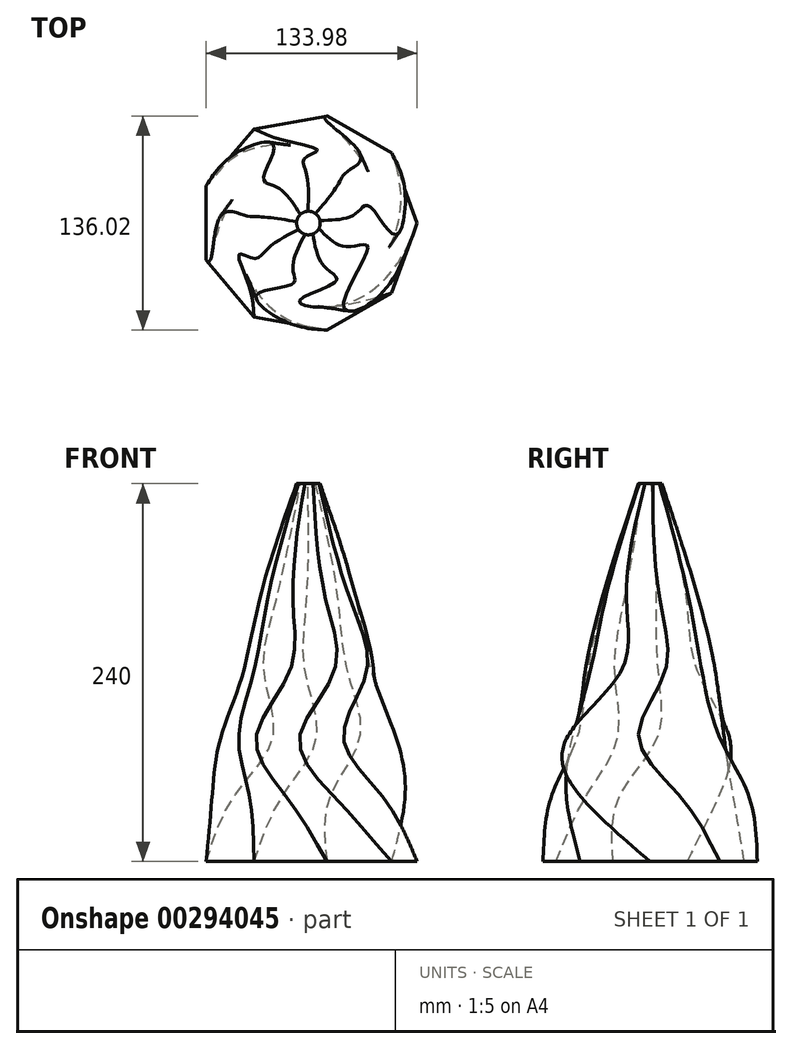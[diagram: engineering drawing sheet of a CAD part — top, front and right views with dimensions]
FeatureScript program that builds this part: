
annotation { "Feature Type Name" : "Feature", "Feature Type Description" : "" }
export const myFeature = defineFeature(function(context is Context, id is Id, definition is map)
    precondition{}
    {
        {
            var Q0;
            Q0=qCreatedBy(makeId("Top.planeOp"),FACE);
            cPlane(context, id + "F0", {"entities" : qUnion([Q0]), "cplaneType" : CPlaneType.OFFSET, "offset" : 40 * mm, "width" : 150 * mm, "height" : 150 * mm});
        }
        {
            var Q0;
            Q0=qCreatedBy(id+"F0.planeOp",FACE);
            cPlane(context, id + "F1", {"entities" : qUnion([Q0]), "cplaneType" : CPlaneType.OFFSET, "offset" : 40 * mm, "width" : 150 * mm, "height" : 150 * mm});
        }
        {
            var Q0;
            Q0=qCreatedBy(id+"F1.planeOp",FACE);
            cPlane(context, id + "F2", {"entities" : qUnion([Q0]), "cplaneType" : CPlaneType.OFFSET, "offset" : 40 * mm, "width" : 150 * mm, "height" : 150 * mm});
        }
        {
            var Q0;
            Q0=qCreatedBy(makeId("Top.planeOp"),FACE);
            var sketch = newSketch(context, id + "F3", { "sketchPlane" : qUnion([Q0])});
            skCircle(sketch, "E0.cCircle", {"center": v(0, 0) * mm, "radius": 64.9 * mm, "construction": true});
            skLineSegment(sketch, "E0.0", {"start": v(12.06, 68) * mm, "end": v(52.95, 44.34) * mm});
            skLineSegment(sketch, "E0.1", {"start": v(52.95, 44.34) * mm, "end": v(69.06, -0.07) * mm});
            skLineSegment(sketch, "E0.2", {"start": v(69.06, -0.07) * mm, "end": v(52.86, -44.45) * mm});
            skLineSegment(sketch, "E0.3", {"start": v(52.86, -44.45) * mm, "end": v(11.92, -68.02) * mm});
            skLineSegment(sketch, "E0.4", {"start": v(11.92, -68.02) * mm, "end": v(-34.6, -59.77) * mm});
            skLineSegment(sketch, "E0.5", {"start": v(-34.6, -59.77) * mm, "end": v(-64.92, -23.55) * mm});
            skLineSegment(sketch, "E0.6", {"start": v(-64.92, -23.55) * mm, "end": v(-64.87, 23.69) * mm});
            skLineSegment(sketch, "E0.7", {"start": v(-64.87, 23.69) * mm, "end": v(-34.47, 59.84) * mm});
            skLineSegment(sketch, "E0.8", {"start": v(-34.47, 59.84) * mm, "end": v(12.06, 68) * mm});
            skPoint(sketch, "E0.0.midPoint", {"position": v(32.5, 56.17) * mm});
            skSolve(sketch);
        }
        {
            var Q0;
            Q0=qCreatedBy(id+"F0.planeOp",FACE);
            var sketch = newSketch(context, id + "F4", { "sketchPlane" : qUnion([Q0])});
            skCircle(sketch, "E1.cCircle", {"center": v(0, 0) * mm, "radius": 55.87 * mm, "construction": true});
            skLineSegment(sketch, "E1.0", {"start": v(13.21, 63.15) * mm, "end": v(61.3, 20.13) * mm});
            skLineSegment(sketch, "E1.1", {"start": v(61.3, 20.13) * mm, "end": v(48.08, -43.02) * mm});
            skLineSegment(sketch, "E1.2", {"start": v(48.08, -43.02) * mm, "end": v(-13.21, -63.15) * mm});
            skLineSegment(sketch, "E1.3", {"start": v(-13.21, -63.15) * mm, "end": v(-61.3, -20.13) * mm});
            skLineSegment(sketch, "E1.4", {"start": v(-61.3, -20.13) * mm, "end": v(-48.08, 43.02) * mm});
            skLineSegment(sketch, "E1.5", {"start": v(-48.08, 43.02) * mm, "end": v(13.21, 63.15) * mm});
            skPoint(sketch, "E1.0.midPoint", {"position": v(37.25, 41.64) * mm});
            skSolve(sketch);
        }
        {
            var Q0;
            Q0=qCreatedBy(id+"F1.planeOp",FACE);
            var sketch = newSketch(context, id + "F5", { "sketchPlane" : qUnion([Q0])});
            skCircle(sketch, "E2.cCircle", {"center": v(0, -1.08) * mm, "radius": 55.64 * mm, "construction": true});
            skLineSegment(sketch, "E2.0", {"start": v(33.08, 43.65) * mm, "end": v(55.28, -7.36) * mm});
            skLineSegment(sketch, "E2.1", {"start": v(55.28, -7.36) * mm, "end": v(22.2, -52.1) * mm});
            skLineSegment(sketch, "E2.2", {"start": v(22.2, -52.1) * mm, "end": v(-33.08, -45.81) * mm});
            skLineSegment(sketch, "E2.3", {"start": v(-33.08, -45.81) * mm, "end": v(-55.28, 5.2) * mm});
            skLineSegment(sketch, "E2.4", {"start": v(-55.28, 5.2) * mm, "end": v(-22.2, 49.94) * mm});
            skLineSegment(sketch, "E2.5", {"start": v(-22.2, 49.94) * mm, "end": v(33.08, 43.65) * mm});
            skSolve(sketch);
        }
        {
            var Q0;
            Q0=qCreatedBy(id+"F2.planeOp",FACE);
            var sketch = newSketch(context, id + "F6", { "sketchPlane" : qUnion([Q0])});
            skCircle(sketch, "E3", {"center": v(0, 0) * mm, "radius": 41.5 * mm});
            skSolve(sketch);
        }
        {
            var Q0;
            Q0=qCreatedBy(id+"F2.planeOp",FACE);
            cPlane(context, id + "F7", {"entities" : qUnion([Q0]), "cplaneType" : CPlaneType.OFFSET, "offset" : 40 * mm, "width" : 150 * mm, "height" : 150 * mm});
        }
        {
            var Q0;
            Q0=qCreatedBy(id+"F7.planeOp",FACE);
            var sketch = newSketch(context, id + "F8", { "sketchPlane" : qUnion([Q0])});
            skCircle(sketch, "E4", {"center": v(0, 0) * mm, "radius": 32.5 * mm});
            skSolve(sketch);
        }
        {
            var Q0;
            Q0=qCreatedBy(id+"F7.planeOp",FACE);
            cPlane(context, id + "F9", {"entities" : qUnion([Q0]), "cplaneType" : CPlaneType.OFFSET, "offset" : 40 * mm, "width" : 150 * mm, "height" : 150 * mm});
        }
        {
            var Q0;
            Q0=qCreatedBy(id+"F9.planeOp",FACE);
            cPlane(context, id + "F10", {"entities" : qUnion([Q0]), "cplaneType" : CPlaneType.OFFSET, "offset" : 40 * mm, "width" : 150 * mm, "height" : 150 * mm});
        }
        {
            var Q0;
            Q0=qCreatedBy(id+"F10.planeOp",FACE);
            var sketch = newSketch(context, id + "F11", { "sketchPlane" : qUnion([Q0])});
            skCircle(sketch, "E5", {"center": v(0, 0) * mm, "radius": 7.5 * mm});
            skSolve(sketch);
        }
        {
            var Q0;
            Q0=makeQuery(id+"F3.imprint","IMPRINT",FACE,{"disambiguationData":[TD([[makeQuery(id+"F3.imprint","IMPRINT",EDGE,{"derivedFrom":sQuery(id+"F3.wireOp",EDGE,"E0.0")}),-1.0]])]});
            var Q1;
            Q1=makeQuery(id+"F4.imprint","IMPRINT",FACE,{"disambiguationData":[TD([[makeQuery(id+"F4.imprint","IMPRINT",EDGE,{"derivedFrom":sQuery(id+"F4.wireOp",EDGE,"E1.0")}),-1.0]])]});
            var Q2;
            Q2=makeQuery(id+"F5.imprint","IMPRINT",FACE,{"disambiguationData":[TD([[makeQuery(id+"F5.imprint","IMPRINT",EDGE,{"derivedFrom":sQuery(id+"F5.wireOp",EDGE,"E2.0")}),-1.0]])]});
            var Q3;
            Q3=makeQuery(id+"F6.imprint","IMPRINT",FACE,{"disambiguationData":[TD([[makeQuery(id+"F6.imprint","IMPRINT",EDGE,{"derivedFrom":sQuery(id+"F6.wireOp",EDGE,"E3")}),1.0]])]});
            var Q4;
            Q4=makeQuery(id+"F8.imprint","IMPRINT",FACE,{"disambiguationData":[TD([[makeQuery(id+"F8.imprint","IMPRINT",EDGE,{"derivedFrom":sQuery(id+"F8.wireOp",EDGE,"E4")}),1.0]])]});
            var Q5;
            Q5=makeQuery(id+"F11.imprint","IMPRINT",FACE,{"disambiguationData":[TD([[makeQuery(id+"F11.imprint","IMPRINT",EDGE,{"derivedFrom":sQuery(id+"F11.wireOp",EDGE,"E5")}),1.0]])]});
            loft(context, id + "F12", {"sheetProfilesArray" : [{ "sheetProfileEntities" : qUnion([Q0]) }, { "sheetProfileEntities" : qUnion([Q1]) }, { "sheetProfileEntities" : qUnion([Q2]) }, { "sheetProfileEntities" : qUnion([Q3]) }, { "sheetProfileEntities" : qUnion([Q4]) }, { "sheetProfileEntities" : qUnion([Q5]) }]});
        }
    });
